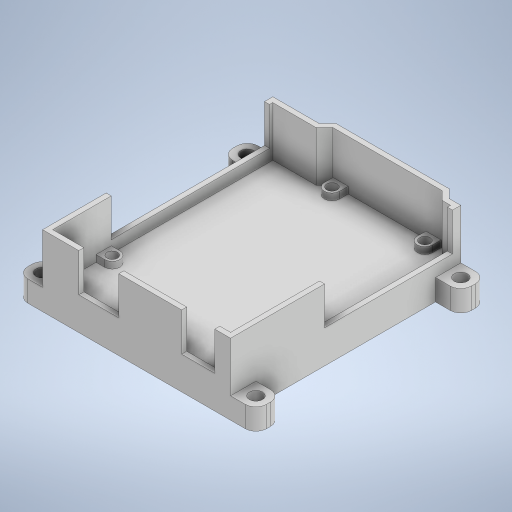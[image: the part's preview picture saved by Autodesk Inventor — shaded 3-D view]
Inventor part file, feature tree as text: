
AUTODESK INVENTOR PART (.ipt)
format: ipt  version: 2024 (Build 280153000, 153)  size: 824,320 bytes
history: native  units: in
note: dims shown in document units (in); Inventor stores cm internally (conversion verified against a paired STEP export)
features: extrude x13, sketch x10, projected_geometry x8
ambient origin geometry x8: Origin, YZ Plane, XZ Plane, XY Plane, X Axis, Y Axis, Z Axis, Center Point
bodies: Solid1 (feature_tree)
feature tree (31):
  extrude  "Extrusion1"  Depth=0.0625in
  extrude  "Extrusion2"  Depth=0.0625in
  extrude  "Extrusion3"  Depth=0.0625in
  extrude  "Extrusion4"  Depth=0.0625in
  extrude  "Extrusion5"  Depth=0.3in
  extrude  "Extrusion6"  Depth=0.3in
  extrude  "Extrusion8"  Depth=0.3in
  sketch  "Sketch6"  dims[d6=0.0625in d7=0.0625in]
  extrude  "Extrusion10"  Depth=0.3in
  extrude  "Extrusion11"  Depth=0.3in
  extrude  "Extrusion12"  Depth=0.098in
  extrude  "Extrusion13"  Depth=0.125in
  extrude  "Extrusion14"  Depth=0.125in TaperAngle=0.0deg
  extrude  "Extrusion15"  Depth=0.125in TaperAngle=0.0deg
  sketch  "Sketch3"  dims[d0=0.0625in d1=0.0625in]
  projected_geometry  "Projected Loop1"
  sketch  "Sketch4"  dims[d2=0.0625in d3=0.0625in]
  projected_geometry  "Projected Loop2"
  sketch  "Sketch5"  dims[d4=0.0625in d5=0.0625in]
  projected_geometry  "Projected Loop3"
  projected_geometry  "Projected Loop4"
  projected_geometry  "Projected Loop6"
  projected_geometry  "Projected Loop8"
  projected_geometry  "Projected Loop11"
  projected_geometry  "Projected Loop12"
  sketch  "Sketch8"  dims[d8=0.3in d9=0.3in]
  sketch  "Sketch9"  dims[d10=0.1575in d11=0.3in]
  sketch  "Sketch10"  dims[d12=0.3in d13=0.3in]
  sketch  "Sketch11"  dims[d14=0.3in d15=0.3in]
  sketch  "Sketch12"  dims[d16=0.3in d17=0.1575in]
  sketch  "Sketch13"  dims[d18=0.1575in d19=0.1575in d20=0.125in d21=0.125in d22=0.0in d23=0.125in d24=0.0in d25=0.125in d26=0.0in d27=0.0in d28=0.0in d29=0.06in d30=0.5906in d31=0.0in d32=0.0in d33=0.0in d36=0.18in d37=0.18in d38=0.18in d39=0.18in d40=0.0787in d41=0.0in d44=1.0in d45=0.0in d46=0.25in d47=0.0in d48=0.1378in d49=0.0in d50=1.0in d51=0.0in d52=0.45in d53=0.0in d54=0.098in d55=1.0in d56=0.0in]
